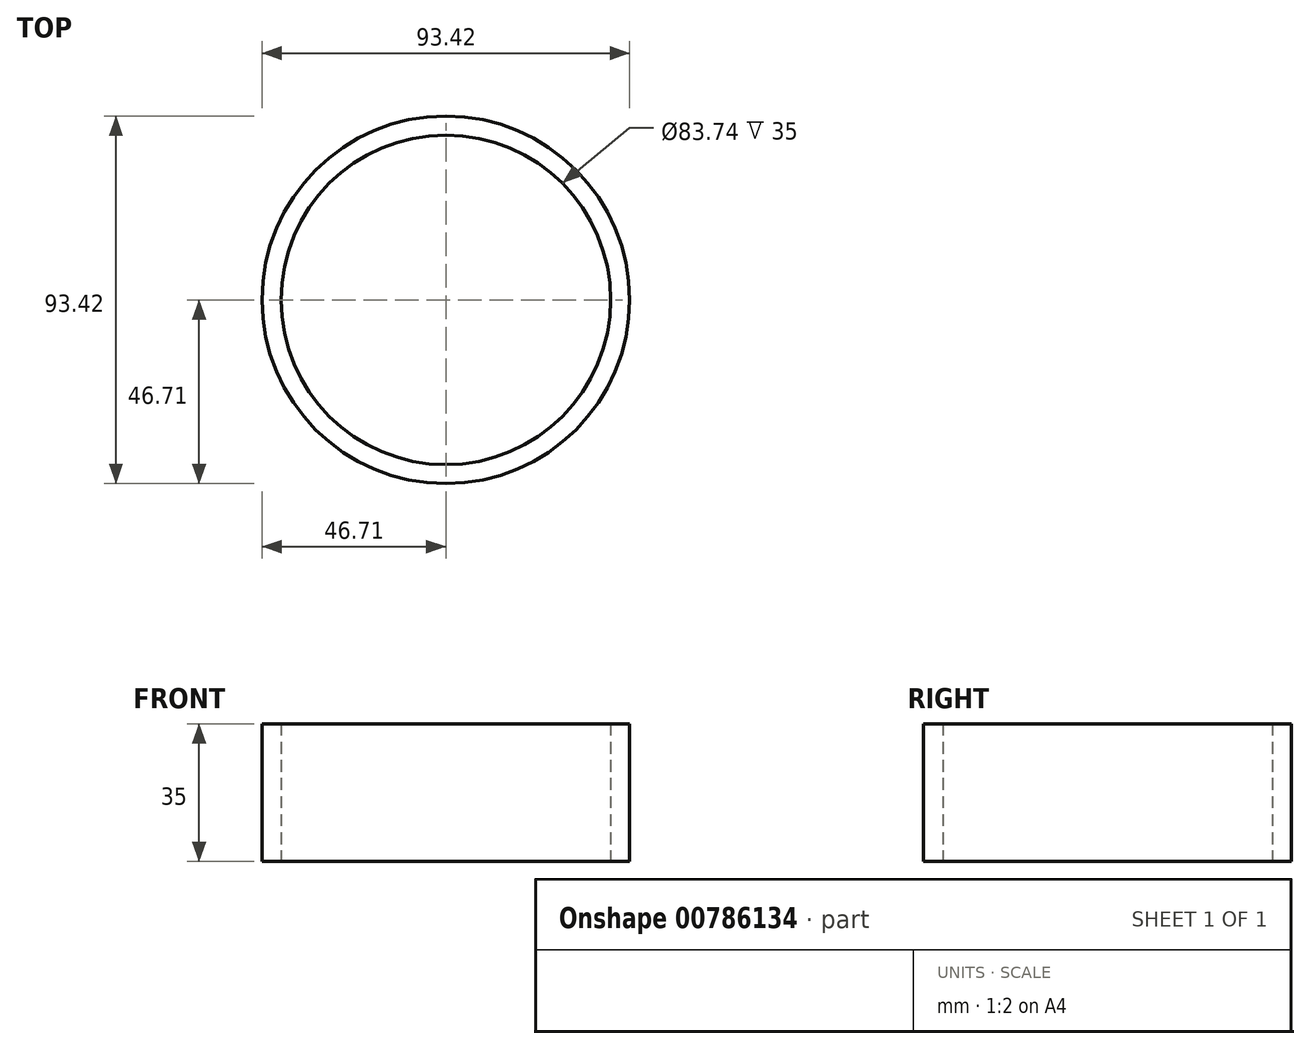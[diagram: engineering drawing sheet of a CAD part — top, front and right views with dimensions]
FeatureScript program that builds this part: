
annotation { "Feature Type Name" : "Feature", "Feature Type Description" : "" }
export const myFeature = defineFeature(function(context is Context, id is Id, definition is map)
    precondition{}
    {
        {
            var Q0;
            Q0=qCreatedBy(makeId("Top.planeOp"),FACE);
            var sketch = newSketch(context, id + "F0", { "sketchPlane" : qUnion([Q0])});
            skCircle(sketch, "E0", {"center": v(0, 0) * mm, "radius": 60.85 * mm});
            skCircle(sketch, "E1", {"center": v(0, 0) * mm, "radius": 28.04 * mm});
            skCircle(sketch, "E2", {"center": v(0, 0) * mm, "radius": 46.7 * mm});
            skCircle(sketch, "E3", {"center": v(0, 0) * mm, "radius": 41.87 * mm});
            skSolve(sketch);
        }
        {
            var Q0;
            Q0=makeQuery(id+"F0.imprint","IMPRINT",FACE,{"disambiguationData":[TD([[makeQuery(id+"F0.imprint","IMPRINT",EDGE,{"derivedFrom":sQuery(id+"F0.wireOp",EDGE,"E2")}),1.0]])]});
            extrude(context, id + "F1", {"entities" : qUnion([Q0]), "depth" : 25 * mm, "hasOffset" : true, "offsetDistance" : 10 * mm, "hasSecondDirection" : true, "secondDirectionOppositeDirection" : true, "secondDirectionDepth" : 10 * mm});
        }
    });
